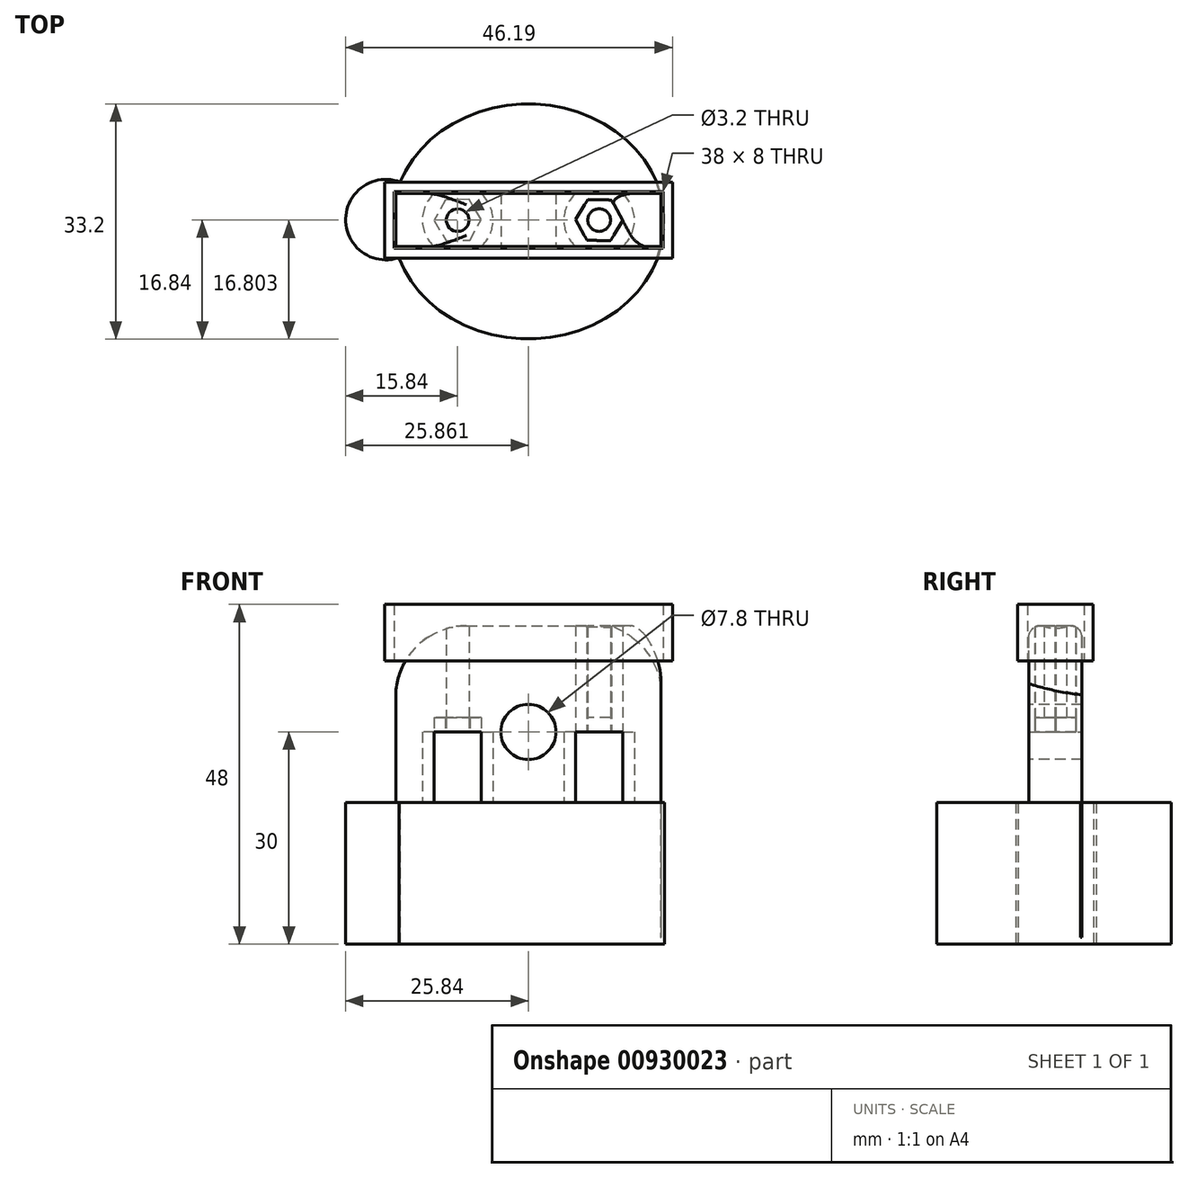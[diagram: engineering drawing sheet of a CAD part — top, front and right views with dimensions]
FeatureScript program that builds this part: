
annotation { "Feature Type Name" : "Feature", "Feature Type Description" : "" }
export const myFeature = defineFeature(function(context is Context, id is Id, definition is map)
    precondition{}
    {
        {
            var Q0;
            Q0=qCreatedBy(makeId("Top.planeOp"),FACE);
            var sketch = newSketch(context, id + "F0", { "sketchPlane" : qUnion([Q0])});
            skLineSegment(sketch, "E0.bottom", {"start": v(-18.75, 7.71) * mm, "end": v(18.75, 7.71) * mm});
            skLineSegment(sketch, "E0.top", {"start": v(-18.75, 0.21) * mm, "end": v(18.75, 0.21) * mm});
            skLineSegment(sketch, "E0.left", {"start": v(-18.75, 7.71) * mm, "end": v(-18.75, 0.21) * mm});
            skLineSegment(sketch, "E0.right", {"start": v(18.75, 7.71) * mm, "end": v(18.75, 0.21) * mm});
            skSolve(sketch);
        }
        {
            var Q0;
            Q0 = qSketchRegion(id + "F0", true);
            extrude(context, id + "F1", {"entities" : qUnion([Q0]), "depth" : 45 * mm, "offsetDistance" : 25 * mm, "hasSecondDirection" : true, "secondDirectionOppositeDirection" : false, "secondDirectionDepth" : 1 * mm});
        }
        {
            var Q0;
            Q0=makeQuery(id+"F1.opExtrude","SWEPT_FACE",FACE,{"disambiguationData":[OSD([sQuery(id+"F0.wireOp",EDGE,"E0.top")])]});
            var sketch = newSketch(context, id + "F2", { "sketchPlane" : qUnion([Q0])});
            skCircle(sketch, "E1", {"center": v(0, 30) * mm, "radius": 3.9 * mm});
            skCircle(sketch, "E2", {"center": v(-7.85, 8) * mm, "radius": 3.9 * mm});
            skCircle(sketch, "E3.MirrorC", {"center": v(7.85, 8) * mm, "radius": 3.9 * mm});
            skLineSegment(sketch, "E4", {"start": v(-7.85, 8) * mm, "end": v(7.85, 8) * mm, "construction": true});
            skSolve(sketch);
        }
        {
            var Q0;
            Q0 = qSketchRegion(id + "F2", true);
            extrude(context, id + "F3", {"entities" : qUnion([Q0]), "operationType" : NewBodyOperationType.REMOVE, "oppositeDirection" : true, "depth" : 25 * mm, "offsetDistance" : 25 * mm});
        }
        {
            var Q0;
            Q0=qCreatedBy(makeId("Top.planeOp"),FACE);
            var sketch = newSketch(context, id + "F4", { "sketchPlane" : qUnion([Q0])});
            skCircle(sketch, "E5", {"center": v(-10, 3.96) * mm, "radius": 1.6 * mm});
            skCircle(sketch, "E6.MirrorC", {"center": v(10, 3.96) * mm, "radius": 1.6 * mm});
            skCircle(sketch, "E7", {"center": v(10, 3.96) * mm, "radius": 5 * mm});
            skCircle(sketch, "E8", {"center": v(-10, 3.96) * mm, "radius": 5 * mm});
            skCircle(sketch, "E9.cCircle", {"center": v(-10, 3.96) * mm, "radius": 2.88 * mm, "construction": true});
            skLineSegment(sketch, "E9.0", {"start": v(-8.4, 6.87) * mm, "end": v(-6.68, 4.03) * mm});
            skLineSegment(sketch, "E9.1", {"start": v(-6.68, 4.03) * mm, "end": v(-8.28, 1.12) * mm});
            skLineSegment(sketch, "E9.2", {"start": v(-8.28, 1.12) * mm, "end": v(-11.6, 1.05) * mm});
            skLineSegment(sketch, "E9.3", {"start": v(-11.6, 1.05) * mm, "end": v(-13.32, 3.9) * mm});
            skLineSegment(sketch, "E9.4", {"start": v(-13.32, 3.9) * mm, "end": v(-11.72, 6.8) * mm});
            skLineSegment(sketch, "E9.5", {"start": v(-11.72, 6.8) * mm, "end": v(-8.4, 6.87) * mm});
            skPoint(sketch, "E9.0.midPoint", {"position": v(-7.54, 5.45) * mm});
            skLineSegment(sketch, "E10.MirrorCS", {"start": v(6.68, 4.03) * mm, "end": v(8.28, 1.12) * mm});
            skLineSegment(sketch, "E11.MirrorCS", {"start": v(8.4, 6.87) * mm, "end": v(6.68, 4.03) * mm});
            skLineSegment(sketch, "E12.MirrorCS", {"start": v(11.72, 6.8) * mm, "end": v(8.4, 6.87) * mm});
            skLineSegment(sketch, "E13.MirrorCS", {"start": v(13.32, 3.9) * mm, "end": v(11.72, 6.8) * mm});
            skLineSegment(sketch, "E14.MirrorCS", {"start": v(11.6, 1.05) * mm, "end": v(13.32, 3.9) * mm});
            skLineSegment(sketch, "E15.MirrorCS", {"start": v(8.28, 1.12) * mm, "end": v(11.6, 1.05) * mm});
            skSolve(sketch);
        }
        {
            var Q0;
            Q0=makeQuery(id+"F4.imprint","IMPRINT",FACE,{"disambiguationData":[TD([[makeQuery(id+"F4.imprint","IMPRINT",EDGE,{"derivedFrom":sQuery(id+"F4.wireOp",EDGE,"E6.MirrorC")}),-1.0]])]});
            var Q1;
            Q1=makeQuery(id+"F4.imprint","IMPRINT",FACE,{"disambiguationData":[TD([[makeQuery(id+"F4.imprint","IMPRINT",EDGE,{"derivedFrom":sQuery(id+"F4.wireOp",EDGE,"E5")}),1.0]])]});
            extrude(context, id + "F5", {"entities" : qUnion([Q0, Q1]), "operationType" : NewBodyOperationType.REMOVE, "depth" : 50 * mm, "offsetDistance" : 25 * mm});
        }
        {
            var Q0;
            Q0 = qSketchRegion(id + "F4", true);
            var Q1;
            Q1=makeQuery(id+"F4.imprint","IMPRINT",FACE,{"disambiguationData":[TD([[makeQuery(id+"F4.imprint","IMPRINT",EDGE,{"derivedFrom":sQuery(id+"F4.wireOp",EDGE,"E5")}),-1.0]])]});
            var Q2;
            Q2=makeQuery(id+"F4.imprint","IMPRINT",FACE,{"disambiguationData":[TD([[makeQuery(id+"F4.imprint","IMPRINT",EDGE,{"derivedFrom":sQuery(id+"F4.wireOp",EDGE,"E6.MirrorC")}),1.0]])]});
            extrude(context, id + "F6", {"entities" : qUnion([Q0, Q1, Q2]), "operationType" : NewBodyOperationType.REMOVE, "depth" : 30 * mm, "offsetDistance" : 25 * mm});
        }
        {
            var Q0;
            Q0=makeQuery(id+"F4.imprint","IMPRINT",FACE,{"disambiguationData":[TD([[makeQuery(id+"F4.imprint","IMPRINT",EDGE,{"derivedFrom":sQuery(id+"F4.wireOp",EDGE,"E5")}),-1.0]])]});
            var Q1;
            Q1=makeQuery(id+"F4.imprint","IMPRINT",FACE,{"disambiguationData":[TD([[makeQuery(id+"F4.imprint","IMPRINT",EDGE,{"derivedFrom":sQuery(id+"F4.wireOp",EDGE,"E6.MirrorC")}),1.0]])]});
            extrude(context, id + "F7", {"entities" : qUnion([Q0, Q1]), "operationType" : NewBodyOperationType.REMOVE, "depth" : 32 * mm, "offsetDistance" : 25 * mm});
        }
        {
            var Q0;
            Q0=makeQuery(id+"F1.opExtrude","CAP_EDGE",EDGE,{"disambiguationData":[OSD([sQuery(id+"F0.wireOp",EDGE,"E0.bottom")])],"isStart":false});
            var Q1;
            Q1=makeQuery(id+"F1.opExtrude","CAP_EDGE",EDGE,{"disambiguationData":[OSD([sQuery(id+"F0.wireOp",EDGE,"E0.top")])],"isStart":false});
            fillet(context, id + "F8", {"entities" : qUnion([Q0, Q1]), "radius" : 1.6 * mm, "allowEdgeOverflow" : false});
        }
        {
            var Q0;
            Q0=makeQuery(id+"F1.opExtrude","CAP_EDGE",EDGE,{"disambiguationData":[OSD([sQuery(id+"F0.wireOp",EDGE,"E0.right")])],"isStart":false});
            var Q1;
            Q1=makeQuery(id+"F1.opExtrude","CAP_EDGE",EDGE,{"disambiguationData":[OSD([sQuery(id+"F0.wireOp",EDGE,"E0.left")])],"isStart":false});
            fillet(context, id + "F9", {"entities" : qUnion([Q0, Q1]), "radius" : 10 * mm, "allowEdgeOverflow" : false});
        }
        {
            var Q0;
            Q0=qCreatedBy(makeId("Top.planeOp"),FACE);
            var sketch = newSketch(context, id + "F10", { "sketchPlane" : qUnion([Q0])});
            skLineSegment(sketch, "E16.bottom", {"start": v(-20.35, 9.31) * mm, "end": v(20.35, 9.31) * mm});
            skLineSegment(sketch, "E16.top", {"start": v(-20.35, -1.39) * mm, "end": v(20.35, -1.39) * mm});
            skLineSegment(sketch, "E16.left", {"start": v(-20.35, 9.31) * mm, "end": v(-20.35, -1.39) * mm});
            skLineSegment(sketch, "E16.right", {"start": v(20.35, 9.31) * mm, "end": v(20.35, -1.39) * mm});
            skLineSegment(sketch, "E17.bottom", {"start": v(-18.98, 8) * mm, "end": v(19.02, 8) * mm});
            skLineSegment(sketch, "E17.top", {"start": v(-18.98, 0) * mm, "end": v(19.02, 0) * mm});
            skLineSegment(sketch, "E17.left", {"start": v(-18.98, 8) * mm, "end": v(-18.98, 0) * mm});
            skLineSegment(sketch, "E17.right", {"start": v(19.02, 8) * mm, "end": v(19.02, 0) * mm});
            skSolve(sketch);
        }
        {
            var Q0;
            Q0 = qSketchRegion(id + "F10", true);
            extrude(context, id + "F11", {"entities" : qUnion([Q0]), "depth" : 48 * mm, "offsetDistance" : 25 * mm, "hasSecondDirection" : true, "secondDirectionOppositeDirection" : false, "secondDirectionDepth" : 40 * mm});
        }
        {
            var Q0;
            Q0=qCreatedBy(makeId("Top.planeOp"),FACE);
            var sketch = newSketch(context, id + "F12", { "sketchPlane" : qUnion([Q0])});
            skEllipse(sketch, "E18", {"center": v(0, 3.76) * mm, "majorRadius": 16.6 * mm, "minorRadius": 19.25 * mm, "majorAxis": v(0, -1)});
            skFitSpline(sketch, "E19.0", {"points": [v(21.58, 1.85) * mm, v(21.69, 3.76) * mm, v(21.58, 5.67) * mm, v(21.14, 8.18) * mm, v(20.3, 10.6) * mm, v(19.05, 12.87) * mm, v(17.55, 15.02) * mm, v(15.27, 17.4) * mm, v(12.53, 19.35) * mm, v(10.09, 20.61) * mm, v(7.54, 21.65) * mm, v(4.86, 22.35) * mm, v(2.1, 22.7) * mm, v(0, 22.8) * mm, v(-2.1, 22.7) * mm, v(-4.86, 22.35) * mm, v(-7.54, 21.65) * mm, v(-10.09, 20.61) * mm, v(-12.53, 19.35) * mm, v(-15.27, 17.4) * mm, v(-17.55, 15.02) * mm, v(-19.05, 12.87) * mm, v(-20.3, 10.6) * mm, v(-21.14, 8.18) * mm, v(-21.58, 5.67) * mm, v(-21.69, 3.76) * mm, v(-21.58, 1.85) * mm, v(-21.14, -0.65) * mm, v(-20.3, -3.07) * mm, v(-19.05, -5.34) * mm, v(-17.55, -7.5) * mm, v(-15.27, -9.88) * mm, v(-12.53, -11.83) * mm, v(-10.09, -13.08) * mm, v(-7.54, -14.12) * mm, v(-4.86, -14.82) * mm, v(-2.1, -15.18) * mm, v(0, -15.27) * mm, v(2.1, -15.18) * mm, v(4.86, -14.82) * mm, v(7.54, -14.12) * mm, v(10.09, -13.08) * mm, v(12.53, -11.83) * mm, v(15.27, -9.88) * mm, v(17.55, -7.5) * mm, v(19.05, -5.34) * mm, v(20.3, -3.07) * mm, v(21.14, -0.65) * mm, v(21.58, 1.85) * mm, v(21.69, 3.76) * mm, v(21.58, 5.67) * mm, v(21.58, 1.85) * mm]});
            skArc(sketch, "E20", {"start": v(-18.13, 9.34) * mm, "mid": v(-25.84, 4.12) * mm, "end": v(-18.31, -1.35) * mm});
            skArc(sketch, "E21.0", {"start": v(-17.56, 10.83) * mm, "mid": v(-27.44, 4.15) * mm, "end": v(-17.8, -2.86) * mm});
            skSolve(sketch);
        }
        {
            var Q0;
            Q0 = qSketchRegion(id + "F12", true);
            extrude(context, id + "F13", {"entities" : qUnion([Q0]), "depth" : 20 * mm, "offsetDistance" : 25 * mm});
        }
        {
            var Q0;
            {var subQ0=sQuery(id+"F12.wireOp",EDGE,"E20");var subQ1=sQuery(id+"F12.wireOp",EDGE,"E19.0");var subQ2=makeQuery(id+"F12.imprint","INTERSECT",VERTEX,{"disambiguationData":[OD(0.0)],"derivedFrom":[subQ1,subQ0]});Q0=makeQuery(id+"F12.imprint","IMPRINT",FACE,{"disambiguationData":[TD([[makeQuery(id+"F12.imprint","IMPRINT",EDGE,{"disambiguationData":[TD([[subQ2,-1.0]])],"derivedFrom":subQ1}),-1.0]])]});}
            var Q1;
            {var subQ0=sQuery(id+"F12.wireOp",EDGE,"E20");var subQ1=sQuery(id+"F12.wireOp",EDGE,"E18");var subQ2=makeQuery(id+"F12.imprint","INTERSECT",VERTEX,{"disambiguationData":[OD(0.0)],"derivedFrom":[subQ1,subQ0]});Q1=makeQuery(id+"F12.imprint","IMPRINT",FACE,{"disambiguationData":[TD([[makeQuery(id+"F12.imprint","IMPRINT",EDGE,{"disambiguationData":[TD([[subQ2,-1.0]])],"derivedFrom":subQ1}),-1.0]])]});}
            extrude(context, id + "F14", {"entities" : qUnion([Q0, Q1]), "operationType" : NewBodyOperationType.ADD, "depth" : 3 * mm, "offsetDistance" : 25 * mm});
        }
    });
